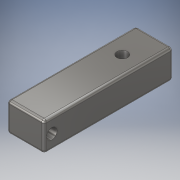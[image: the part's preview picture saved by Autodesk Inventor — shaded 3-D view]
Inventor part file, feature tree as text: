
AUTODESK INVENTOR PART (.ipt)
format: ipt  version: 2018 (Build 220112000, 112)  size: 157,696 bytes
history: native  units: in
note: dims shown in document units (in); Inventor stores cm internally (conversion verified against a paired STEP export)
features: extrude x3, sketch x3, fillet x2
ambient origin geometry x8: Origin, YZ Plane, XZ Plane, XY Plane, X Axis, Y Axis, Z Axis, Center Point
bodies: Solid1 (feature_tree)
feature tree (8):
  extrude  "Extrusion1"  Depth=1.35in
  extrude  "Extrusion3"  Depth=6.0in
  extrude  "Extrusion4"  Depth=0.125in TaperAngle=0.0deg
  fillet  "Fillet1"  Radius=0.5in
  fillet  "Fillet2"  Radius=0.35in
  sketch  "Sketch1"  dims[d0=1.738in d1=1.35in]
  sketch  "Sketch3"  dims[d2=6.0in d3=0.0in d7=0.5in]
  sketch  "Sketch4"  dims[d8=2.0in d9=0.0in d11=5.0in d12=0.0in d14=0.5in d15=0.35in d16=0.125in d17=0.125in]
